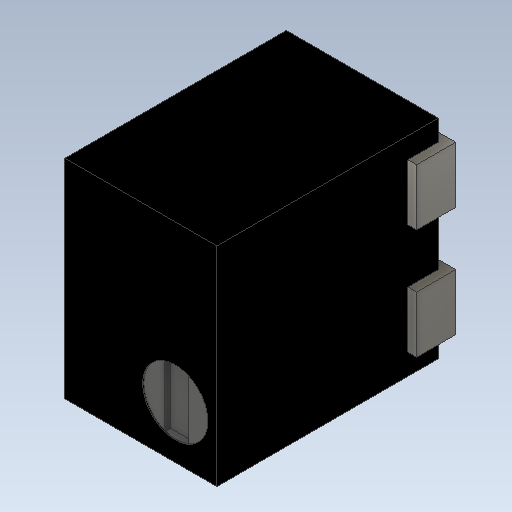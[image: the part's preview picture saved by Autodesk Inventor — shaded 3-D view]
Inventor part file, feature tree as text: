
AUTODESK INVENTOR PART (.ipt)
format: ipt  version: 2020 (Build 240168000, 168)  size: 171,520 bytes
history: native  units: in
note: dims shown in document units (in); Inventor stores cm internally (conversion verified against a paired STEP export)
features: extrude x4, sketch x4, projected_geometry x1
ambient origin geometry x8: Origin, YZ Plane, XZ Plane, XY Plane, X Axis, Y Axis, Z Axis, Center Point
bodies: Solid1 (feature_tree)
feature tree (9):
  extrude  "Extrusion1"  Depth=0.189in
  extrude  "Extrusion2"  Depth=0.0591in
  extrude  "Extrusion3"  Depth=0.1in
  extrude  "Extrusion4"  Depth=0.022in
  sketch  "Sketch1"  dims[d0=0.1378in d1=0.189in]
  sketch  "Sketch2"  dims[d2=0.2008in d3=0.0in d4=0.0591in]
  sketch  "Sketch3"  dims[d5=0.0472in d6=0.1in]
  projected_geometry  "Projected Loop1"
  sketch  "Sketch4"  dims[d7=0.001in d8=0.0in d9=0.022in d10=0.0059in d11=0.0in d12=0.0394in d13=0.0512in d14=0.0079in d15=0.0079in d16=0.1in d17=0.05in d18=0.0079in d19=0.0276in d20=0.0in d21=0.0in]
